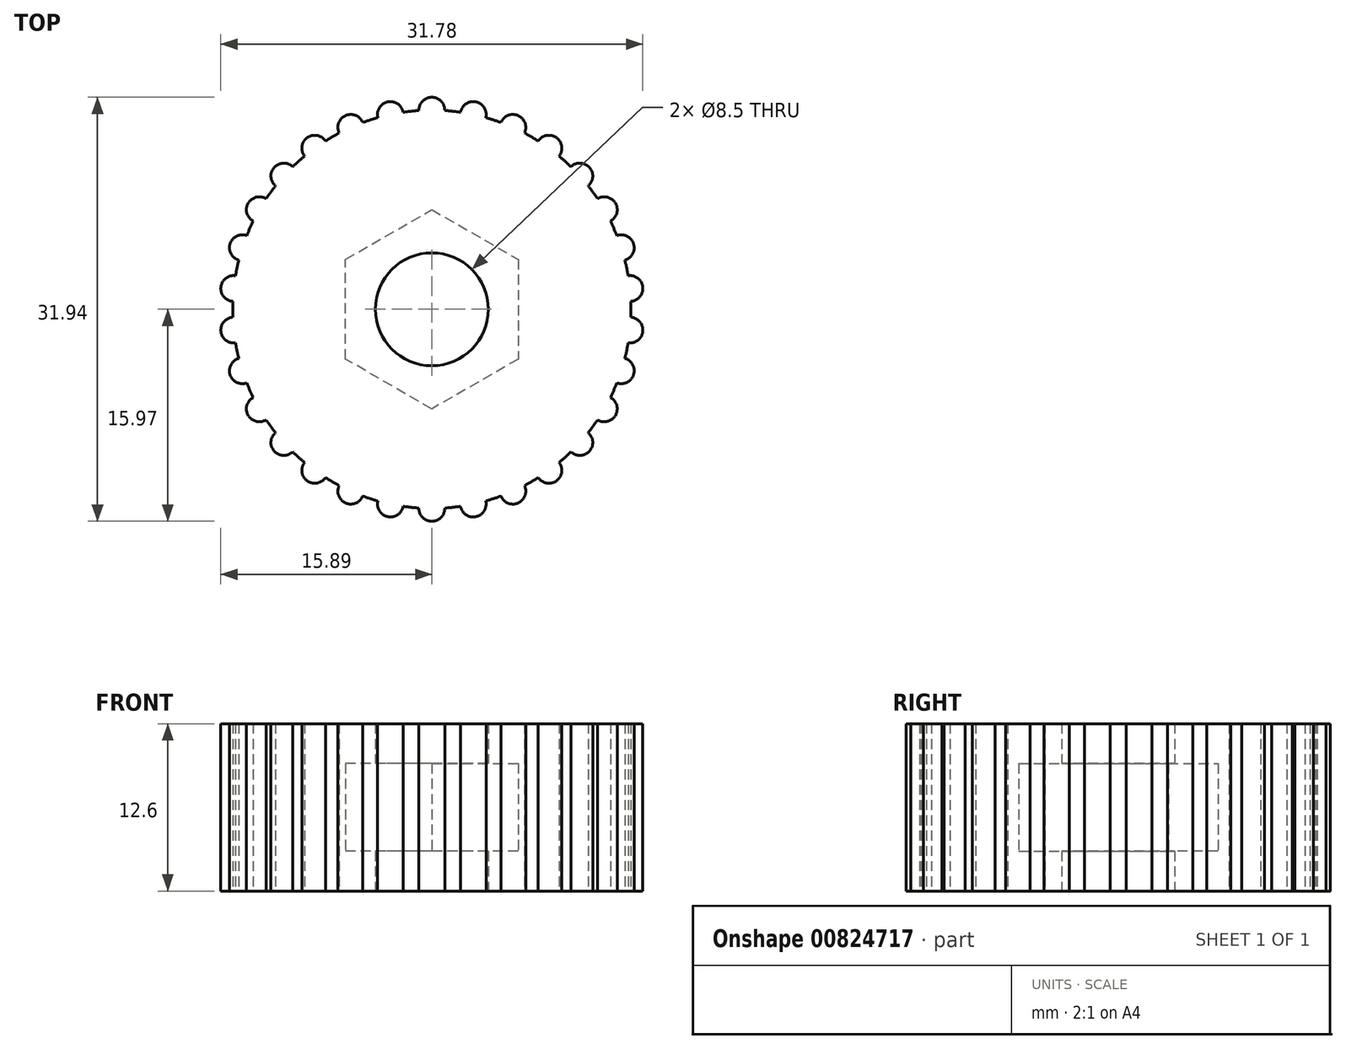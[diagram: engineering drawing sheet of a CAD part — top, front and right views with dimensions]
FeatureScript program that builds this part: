
annotation { "Feature Type Name" : "Feature", "Feature Type Description" : "" }
export const myFeature = defineFeature(function(context is Context, id is Id, definition is map)
    precondition{}
    {
        {
            var Q0;
            Q0=qCreatedBy(makeId("Top.planeOp"),FACE);
            var sketch = newSketch(context, id + "F0", { "sketchPlane" : qUnion([Q0])});
            skCircle(sketch, "E0", {"center": v(0, 0) * mm, "radius": 15 * mm});
            skCircle(sketch, "E1.cCircle", {"center": v(0, 0) * mm, "radius": 6.5 * mm, "construction": true});
            skLineSegment(sketch, "E1.0", {"start": v(6.5, 3.75) * mm, "end": v(6.5, -3.75) * mm});
            skLineSegment(sketch, "E1.1", {"start": v(6.5, -3.75) * mm, "end": v(0, -7.5) * mm});
            skLineSegment(sketch, "E1.2", {"start": v(0, -7.5) * mm, "end": v(-6.5, -3.75) * mm});
            skLineSegment(sketch, "E1.3", {"start": v(-6.5, -3.75) * mm, "end": v(-6.5, 3.75) * mm});
            skLineSegment(sketch, "E1.4", {"start": v(-6.5, 3.75) * mm, "end": v(0, 7.5) * mm});
            skLineSegment(sketch, "E1.5", {"start": v(0, 7.5) * mm, "end": v(6.5, 3.75) * mm});
            skPoint(sketch, "E1.0.midPoint", {"position": v(6.5, 0) * mm});
            skCircle(sketch, "E2", {"center": v(0, 0) * mm, "radius": 4.25 * mm});
            skArc(sketch, "E3", {"start": v(-0.97, -14.97) * mm, "mid": v(0, -15.97) * mm, "end": v(0.97, -14.97) * mm});
            skSolve(sketch);
        }
        {
            var Q0;
            Q0=makeQuery(id+"F0.imprint","IMPRINT",FACE,{"disambiguationData":[TD([[makeQuery(id+"F0.imprint","IMPRINT",EDGE,{"derivedFrom":sQuery(id+"F0.wireOp",EDGE,"E0")}),1.0]])]});
            var Q1;
            Q1=makeQuery(id+"F0.imprint","IMPRINT",FACE,{"disambiguationData":[TD([[makeQuery(id+"F0.imprint","IMPRINT",EDGE,{"derivedFrom":sQuery(id+"F0.wireOp",EDGE,"E1.0")}),-1.0]])]});
            var Q2;
            Q2=makeQuery(id+"F0.imprint","IMPRINT",FACE,{"disambiguationData":[TD([[makeQuery(id+"F0.imprint","IMPRINT",EDGE,{"derivedFrom":sQuery(id+"F0.wireOp",EDGE,"E2")}),1.0]])]});
            extrude(context, id + "F1", {"entities" : qUnion([Q0, Q1, Q2]), "depth" : 3 * mm, "offsetDistance" : 25 * mm});
        }
        {
            var Q0;
            Q0=makeQuery(id+"F1.opExtrude","CAP_FACE",FACE,{"disambiguationData":[OSD([sQuery(id+"F0.wireOp",EDGE,"E0")])],"isStart":false});
            var sketch = newSketch(context, id + "F2", { "sketchPlane" : qUnion([Q0])});
            skLineSegment(sketch, "E4.0", {"start": v(-6.5, 3.75) * mm, "end": v(0, 7.5) * mm});
            skLineSegment(sketch, "E5.0", {"start": v(0, 7.5) * mm, "end": v(6.5, 3.75) * mm});
            skLineSegment(sketch, "E6.0", {"start": v(6.5, 3.75) * mm, "end": v(6.5, -3.75) * mm});
            skLineSegment(sketch, "E7.0", {"start": v(6.5, -3.75) * mm, "end": v(0, -7.5) * mm});
            skLineSegment(sketch, "E8.0", {"start": v(0, -7.5) * mm, "end": v(-6.5, -3.75) * mm});
            skLineSegment(sketch, "E8.1", {"start": v(-6.5, -3.75) * mm, "end": v(-6.5, 3.75) * mm});
            skSolve(sketch);
        }
        {
            var Q0;
            Q0=makeQuery(id+"F2.imprint","IMPRINT",FACE,{"disambiguationData":[TD([[makeQuery(id+"F2.imprint","IMPRINT",EDGE,{"derivedFrom":sQuery(id+"F2.wireOp",EDGE,"E4.0")}),1.0]])]});
            extrude(context, id + "F3", {"entities" : qUnion([Q0]), "operationType" : NewBodyOperationType.ADD, "depth" : 6.6 * mm, "offsetDistance" : 25 * mm});
        }
        {
            var Q0;
            Q0=makeQuery(id+"F3.opExtrude","CAP_FACE",FACE,{"disambiguationData":[OSD([sQuery(id+"F0.wireOp",EDGE,"E0"),sQuery(id+"F2.wireOp",EDGE,"E4.0"),sQuery(id+"F2.wireOp",EDGE,"E5.0"),sQuery(id+"F2.wireOp",EDGE,"E6.0"),sQuery(id+"F2.wireOp",EDGE,"E7.0"),sQuery(id+"F2.wireOp",EDGE,"E8.0"),sQuery(id+"F2.wireOp",EDGE,"E8.1")])],"isStart":false});
            var sketch = newSketch(context, id + "F4", { "sketchPlane" : qUnion([Q0])});
            skCircle(sketch, "E9.0", {"center": v(0, 0) * mm, "radius": 15 * mm});
            skSolve(sketch);
        }
        {
            var Q0;
            Q0=makeQuery(id+"F4.imprint","IMPRINT",FACE,{"disambiguationData":[TD([[makeQuery(id+"F4.imprint","IMPRINT",EDGE,{"derivedFrom":makeQuery(id+"F3.opExtrude","CAP_EDGE",EDGE,{"disambiguationData":[OSD([sQuery(id+"F2.wireOp",EDGE,"E4.0")])],"isStart":false})}),-1.0]])]});
            var Q1;
            Q1=makeQuery(id+"F4.imprint","IMPRINT",FACE,{"disambiguationData":[TD([[makeQuery(id+"F4.imprint","IMPRINT",EDGE,{"derivedFrom":sQuery(id+"F4.wireOp",EDGE,"E9.0")}),1.0]])]});
            extrude(context, id + "F5", {"entities" : qUnion([Q0, Q1]), "operationType" : NewBodyOperationType.ADD, "depth" : 3 * mm, "offsetDistance" : 25 * mm});
        }
        {
            var Q0;
            {var subQ0=sQuery(id+"F0.wireOp",EDGE,"E3");Q0=makeQuery(id+"F0.imprint","IMPRINT",FACE,{"disambiguationData":[TD([[makeQuery(id+"F0.imprint","IMPRINT",EDGE,{"derivedFrom":subQ0}),1.0]])]});}
            var Q1;
            Q1=makeQuery(id+"F5.opExtrude","CAP_FACE",FACE,{"disambiguationData":[OSD([sQuery(id+"F4.wireOp",EDGE,"E9.0")])],"isStart":false});
            extrude(context, id + "F6", {"entities" : qUnion([Q0]), "endBound" : BoundingType.UP_TO_SURFACE, "depth" : 25 * mm, "endBoundEntityFace" : qUnion([Q1]), "offsetDistance" : 25 * mm});
        }
        {
            var Q0;
            Q0=makeQuery(id+"F6.opExtrude","SWEPT_BODY",BODY,{"disambiguationData":[OSD([sQuery(id+"F0.wireOp",EDGE,"E0"),sQuery(id+"F0.wireOp",EDGE,"E3")])]});
            var Q1;
            Q1=sQuery(id+"F0.wireOp",EDGE,"E2");
            circularPattern(context, id + "F7", {"operationType" : NewBodyOperationType.ADD, "entities" : qUnion([Q0]), "axis" : qUnion([Q1]), "angle" : 360 * degree, "instanceCount" : 30, "equalSpace" : true});
        }
        {
            var Q0;
            Q0=makeQuery(id+"F0.imprint","IMPRINT",FACE,{"disambiguationData":[TD([[makeQuery(id+"F0.imprint","IMPRINT",EDGE,{"derivedFrom":sQuery(id+"F0.wireOp",EDGE,"E2")}),1.0]])]});
            extrude(context, id + "F8", {"entities" : qUnion([Q0]), "operationType" : NewBodyOperationType.REMOVE, "depth" : 25 * mm, "offsetDistance" : 25 * mm});
        }
    });
